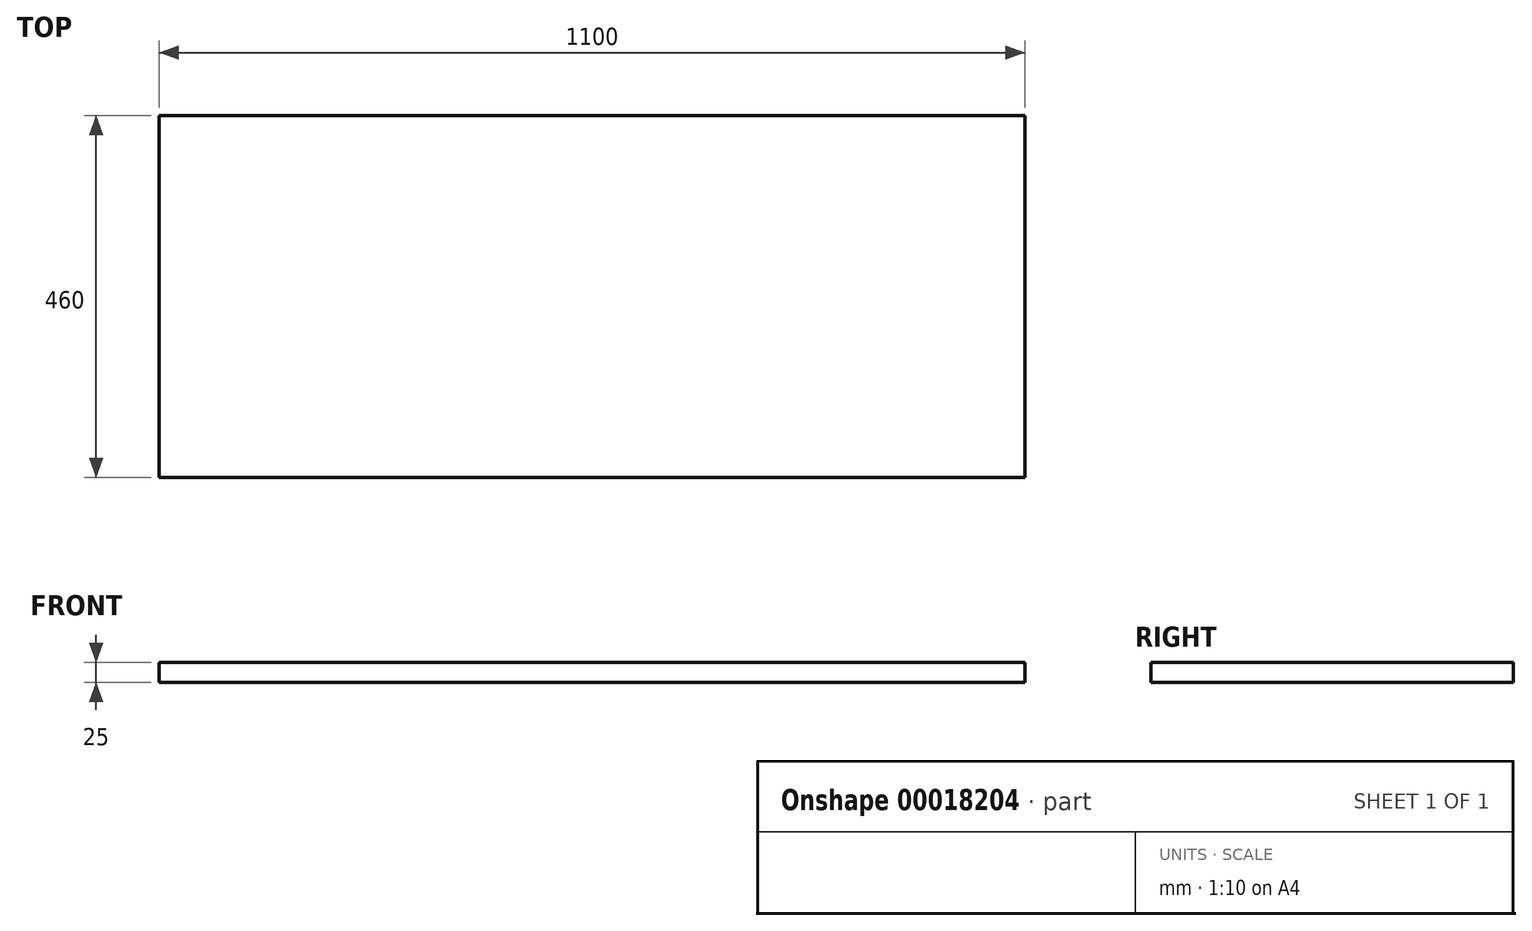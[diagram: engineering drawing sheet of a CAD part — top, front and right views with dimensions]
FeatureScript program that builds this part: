
annotation { "Feature Type Name" : "Feature", "Feature Type Description" : "" }
export const myFeature = defineFeature(function(context is Context, id is Id, definition is map)
    precondition{}
    {
        {
            var Q0;
            Q0=qCreatedBy(makeId("Top.planeOp"),FACE);
            var sketch = newSketch(context, id + "F0", { "sketchPlane" : qUnion([Q0])});
            skLineSegment(sketch, "E0.bottom", {"start": v(0, 0) * mm, "end": v(1100, 0) * mm});
            skLineSegment(sketch, "E0.top", {"start": v(0, 460) * mm, "end": v(1100, 460) * mm});
            skLineSegment(sketch, "E0.left", {"start": v(0, 0) * mm, "end": v(0, 460) * mm});
            skLineSegment(sketch, "E0.right", {"start": v(1100, 0) * mm, "end": v(1100, 460) * mm});
            skSolve(sketch);
        }
        {
            var Q0;
            Q0 = qSketchRegion(id + "F0", true);
            extrude(context, id + "F1", {"entities" : qUnion([Q0]), "depth" : 25 * mm});
        }
    });
